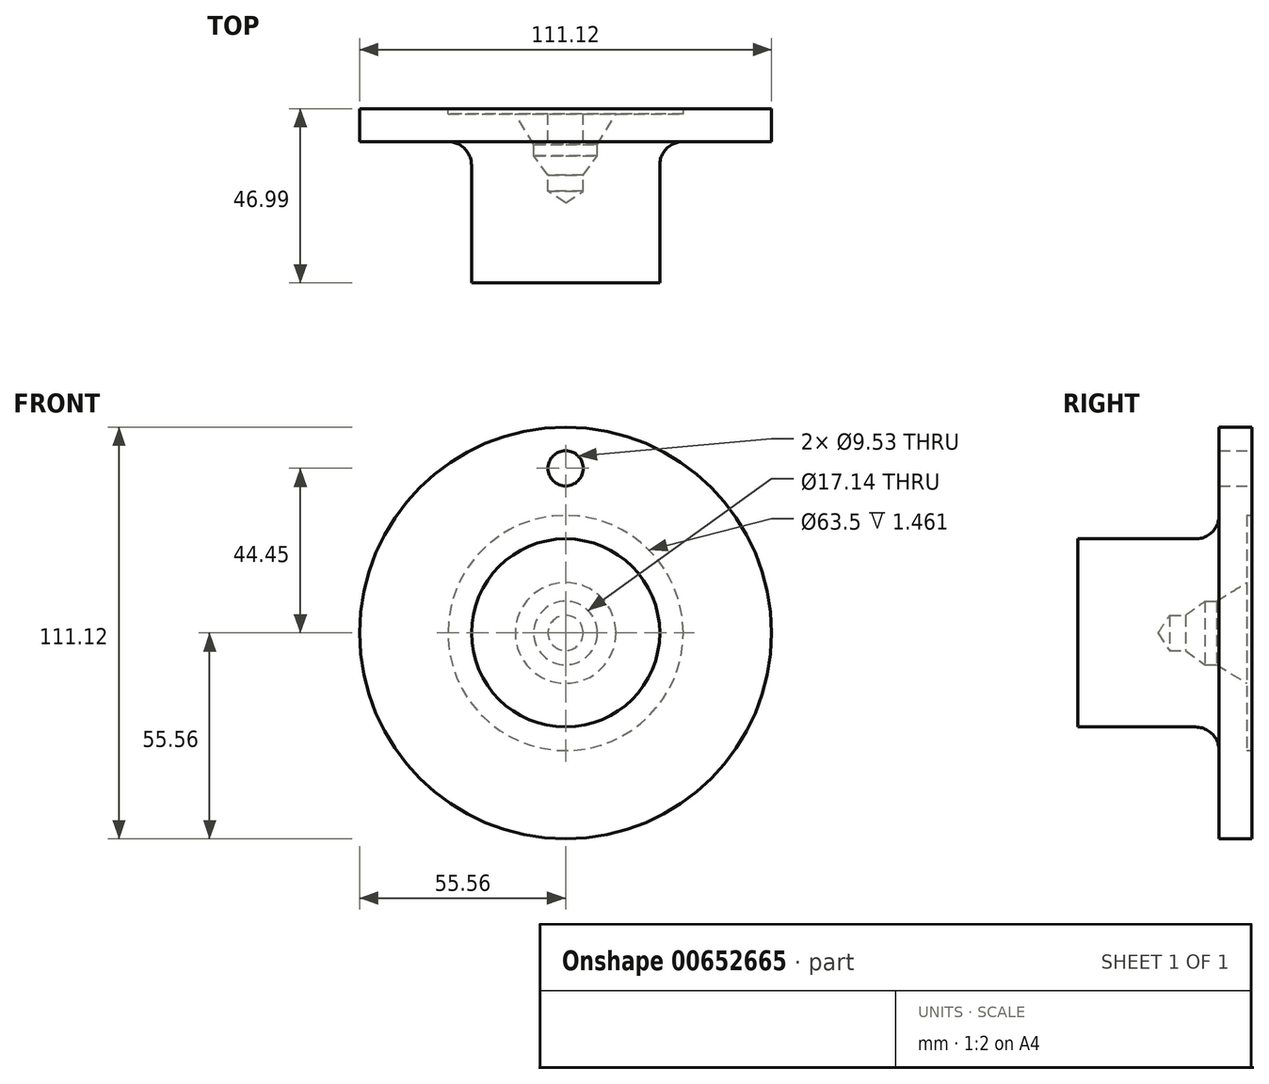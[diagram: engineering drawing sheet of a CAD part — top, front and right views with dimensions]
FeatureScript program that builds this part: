
annotation { "Feature Type Name" : "Feature", "Feature Type Description" : "" }
export const myFeature = defineFeature(function(context is Context, id is Id, definition is map)
    precondition{}
    {
        {
            var Q0;
            Q0=qCreatedBy(makeId("Right.planeOp"),FACE);
            var sketch = newSketch(context, id + "F0", { "sketchPlane" : qUnion([Q0])});
            skLineSegment(sketch, "E0", {"start": v(0, 55.56) * mm, "end": v(8.89, 55.56) * mm});
            skLineSegment(sketch, "E1", {"start": v(8.89, 55.56) * mm, "end": v(8.9, 31.75) * mm});
            skLineSegment(sketch, "E2", {"start": v(8.89, 31.75) * mm, "end": v(7.43, 31.75) * mm});
            skLineSegment(sketch, "E3", {"start": v(7.43, 31.75) * mm, "end": v(7.43, 13.59) * mm});
            skLineSegment(sketch, "E4", {"start": v(7.43, 13.59) * mm, "end": v(-0.74, 8.57) * mm});
            skLineSegment(sketch, "E5", {"start": v(-0.74, 8.57) * mm, "end": v(-3.8, 8.57) * mm});
            skLineSegment(sketch, "E6", {"start": v(-3.81, 8.57) * mm, "end": v(-9.08, 4.76) * mm});
            skLineSegment(sketch, "E7", {"start": v(-9.08, 4.76) * mm, "end": v(-13.33, 4.76) * mm});
            skLineSegment(sketch, "E8", {"start": v(-13.33, 4.76) * mm, "end": v(-16.5, 0) * mm});
            skLineSegment(sketch, "E9", {"start": v(-16.5, 0) * mm, "end": v(-38.1, 0) * mm});
            skLineSegment(sketch, "E10", {"start": v(-38.1, 0) * mm, "end": v(-38.1, 25.4) * mm});
            skLineSegment(sketch, "E11", {"start": v(-38.1, 25.4) * mm, "end": v(-6.35, 25.4) * mm});
            skLineSegment(sketch, "E12", {"start": v(0, 31.75) * mm, "end": v(0, 55.56) * mm});
            skPoint(sketch, "E13.visualSharp", {"position": v(0, 25.4) * mm});
            skArc(sketch, "E13.filletArc", {"start": v(-6.35, 25.4) * mm, "mid": v(-1.86, 27.26) * mm, "end": v(0, 31.75) * mm});
            skSolve(sketch);
        }
        {
            var Q0;
            Q0 = qSketchRegion(id + "F0", true);
            var Q1;
            Q1=sQuery(id+"F0.wireOp",EDGE,"E9");
            revolve(context, id + "F1", {"entities" : qUnion([Q0]), "axis" : qUnion([Q1]), "revolveType" : RevolveType.FULL});
        }
        {
            var Q0;
            Q0=makeQuery(id+"F1.opRevolve","SWEPT_FACE",FACE,{"disambiguationData":[OSD([sQuery(id+"F0.wireOp",EDGE,"E1")])]});
            var sketch = newSketch(context, id + "F2", { "sketchPlane" : qUnion([Q0])});
            skPoint(sketch, "E14", {"position": v(0, 44.45) * mm});
            skSolve(sketch);
        }
        {
            var Q0;
            Q0=sQuery(id+"F2.wireOp",VERTEX,"E14");
            var Q1;
            Q1=makeQuery(id+"F1.opRevolve","SWEPT_BODY",BODY,{"disambiguationData":[OSD([sQuery(id+"F0.wireOp",EDGE,"E0"),sQuery(id+"F0.wireOp",EDGE,"E1"),sQuery(id+"F0.wireOp",EDGE,"E2"),sQuery(id+"F0.wireOp",EDGE,"E3"),sQuery(id+"F0.wireOp",EDGE,"E4"),sQuery(id+"F0.wireOp",EDGE,"E5"),sQuery(id+"F0.wireOp",EDGE,"E6"),sQuery(id+"F0.wireOp",EDGE,"E7"),sQuery(id+"F0.wireOp",EDGE,"E8"),sQuery(id+"F0.wireOp",EDGE,"E9"),sQuery(id+"F0.wireOp",EDGE,"E10"),sQuery(id+"F0.wireOp",EDGE,"E11"),sQuery(id+"F0.wireOp",EDGE,"E12"),sQuery(id+"F0.wireOp",EDGE,"E13.filletArc")])]});
            hole(context, id + "F3", {"style" : HoleStyle.SIMPLE, "endStyle" : HoleEndStyle.THROUGH, "holeDiameter" : 9.52 * mm, "majorDiameter" : 6.35 * mm, "isTappedThrough" : true, "tappedDepth" : 12.7 * mm, "tapClearance" : 3, "locations" : qUnion([Q0]), "scope" : qUnion([Q1])});
        }
    });
